# Revit family: QF_Macom_RVDS-A-2xx
name_source: partatom
category: Specialty Equipment
units: mm (PartAtom-declared; Revit-internal decimal feet)

## family parameters
Always vertical = Yes
Cut with Voids When Loaded = No
OmniClass Number = 23.40.40.11.11.17
OmniClass Title = Refrigerator-Freezer
Part Type = Normal
Room Calculation Point = No
Round Connector Dimension = Use Diameter
Shared = No
Work Plane-Based = No

## types (2) — shared parameters
Default Elevation = 0,00 mm
Depth Actual = 845,00 mm
Door Width = 672,00 mm
Freezer Capacity = 205,0 L
Freezer Work Temperature = -20°C to -16°C
Full_Glass_Door = No
Full_Stainless_Door = No
Half_Glass_Half_Stainless_Door = No
Height Actual = 2070,00 mm
Length Actual = 700,00 mm
Manufacturer = MACOM
Refrigerator Capacity = 230,0 L
Refrigerator Work Temperature = +1°C to +10°C
URL = https://www.acosmacom.com.br
Volts = 220 V
Volume = 1,16 m³
Watts = 751 W
Weight = 150,00 kg

## per-type parameters (varying)
| type | Description | Half_Glass_Door | Half_Stainless_Door |
| RVDS-A-2IG | REFRIGERADOR DUAL TEMP VERTICAL COMERCIAL SIMPLES MACOM, 2 PORTAS INOX-700X800X2070 | No | Yes |
| RVDS-A-2VG | REFRIGERADOR DUAL TEMP VERTICAL COMERCIAL SIMPLES MACOM, 2 PORTAS VIDRO-700X800X2070 | Yes | No |

note: column(s) folded — value = type name in every type: Model

## geometry (parser evidence)
native form markers: Sweep x3
no freeform markers — native parametric forms only
